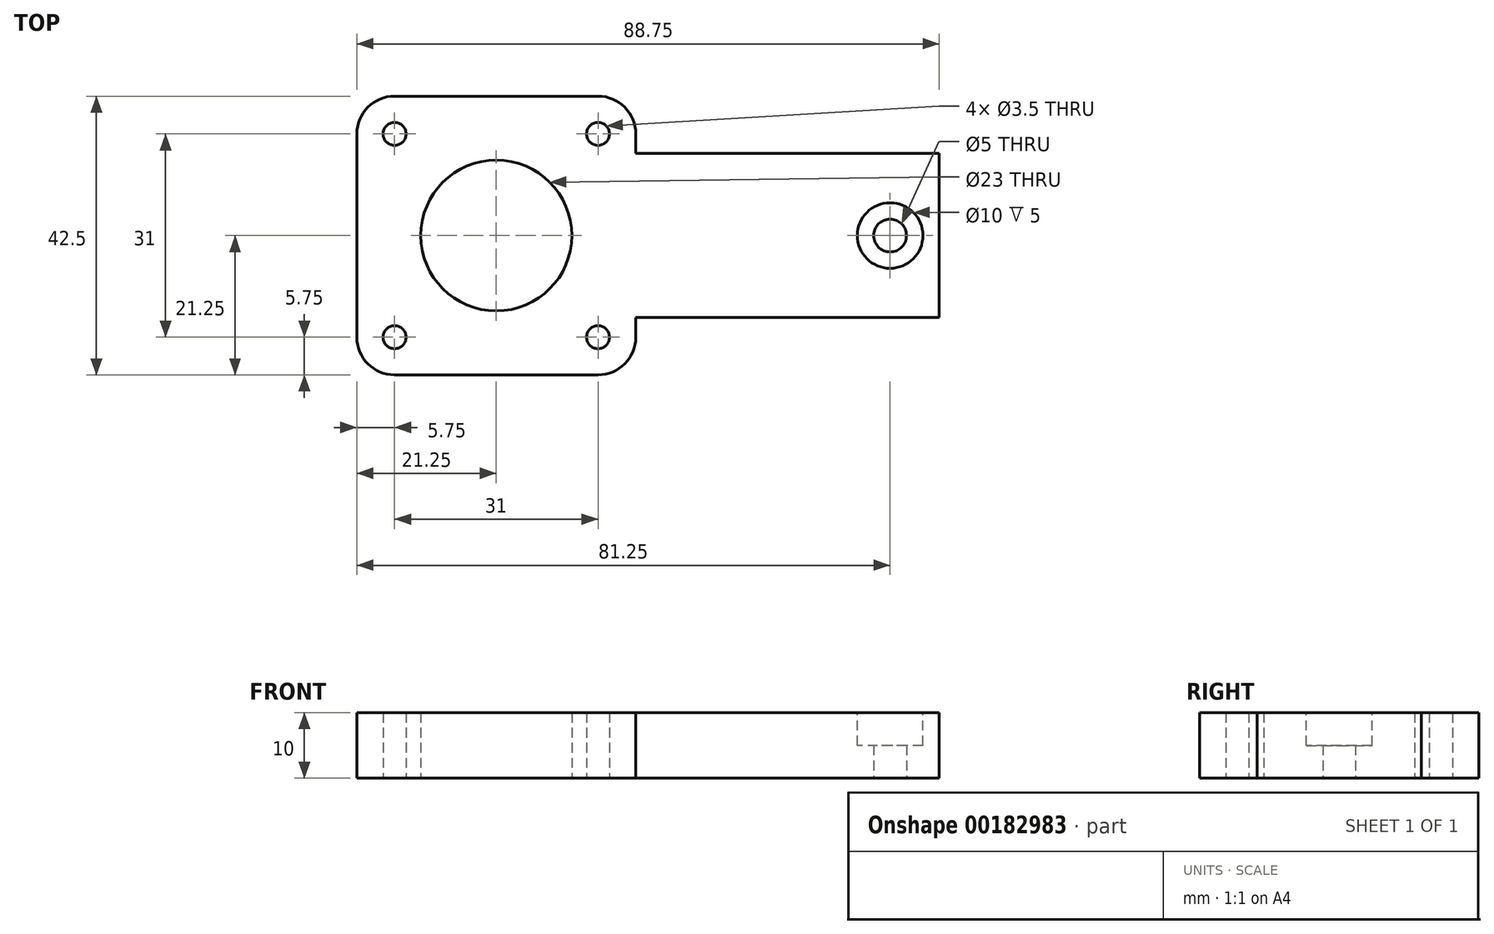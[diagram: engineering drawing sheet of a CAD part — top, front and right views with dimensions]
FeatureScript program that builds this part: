
annotation { "Feature Type Name" : "Feature", "Feature Type Description" : "" }
export const myFeature = defineFeature(function(context is Context, id is Id, definition is map)
    precondition{}
    {
        {
            var Q0;
            Q0=qCreatedBy(makeId("Top.planeOp"),FACE);
            var sketch = newSketch(context, id + "F0", { "sketchPlane" : qUnion([Q0])});
            skCircle(sketch, "E0", {"center": v(0, 0) * mm, "radius": 11.5 * mm});
            skCircle(sketch, "E1", {"center": v(-15.5, 15.5) * mm, "radius": 1.75 * mm});
            skCircle(sketch, "E2", {"center": v(15.5, 15.5) * mm, "radius": 1.75 * mm});
            skCircle(sketch, "E3", {"center": v(15.5, -15.5) * mm, "radius": 1.75 * mm});
            skCircle(sketch, "E4", {"center": v(-15.5, -15.5) * mm, "radius": 1.75 * mm});
            skLineSegment(sketch, "E5.bottom", {"start": v(-21.25, 21.25) * mm, "end": v(21.25, 21.25) * mm});
            skLineSegment(sketch, "E5.top", {"start": v(-21.25, -21.25) * mm, "end": v(21.25, -21.25) * mm});
            skLineSegment(sketch, "E5.left", {"start": v(-21.25, 21.25) * mm, "end": v(-21.25, -21.25) * mm});
            skLineSegment(sketch, "E5.right", {"start": v(21.25, 21.25) * mm, "end": v(21.25, -21.25) * mm});
            skPoint(sketch, "E6", {"position": v(21.25, 0) * mm});
            skCircle(sketch, "E7", {"center": v(60, 0) * mm, "radius": 2.5 * mm});
            skCircle(sketch, "E8", {"center": v(15.5, -15.5) * mm, "radius": 5.75 * mm});
            skCircle(sketch, "E9", {"center": v(15.5, 15.5) * mm, "radius": 5.75 * mm});
            skCircle(sketch, "E10", {"center": v(-15.5, 15.5) * mm, "radius": 5.75 * mm});
            skCircle(sketch, "E11", {"center": v(-15.5, -15.5) * mm, "radius": 5.75 * mm});
            skLineSegment(sketch, "E12.bottom", {"start": v(21.25, 12.5) * mm, "end": v(67.5, 12.5) * mm});
            skLineSegment(sketch, "E12.top", {"start": v(21.25, -12.5) * mm, "end": v(67.5, -12.5) * mm});
            skLineSegment(sketch, "E12.left", {"start": v(21.25, 12.5) * mm, "end": v(21.25, -12.5) * mm});
            skLineSegment(sketch, "E12.right", {"start": v(67.5, 12.5) * mm, "end": v(67.5, -12.5) * mm});
            skPoint(sketch, "E13", {"position": v(67.5, 0) * mm});
            skSolve(sketch);
        }
        {
            var Q0;
            Q0=makeQuery(id+"F0.imprint","IMPRINT",FACE,{"disambiguationData":[TD([[makeQuery(id+"F0.imprint","IMPRINT",EDGE,{"derivedFrom":sQuery(id+"F0.wireOp",EDGE,"E0")}),-1.0]])]});
            var Q1;
            Q1=makeQuery(id+"F0.imprint","IMPRINT",FACE,{"disambiguationData":[TD([[makeQuery(id+"F0.imprint","IMPRINT",EDGE,{"derivedFrom":sQuery(id+"F0.wireOp",EDGE,"E4")}),-1.0]])]});
            var Q2;
            Q2=makeQuery(id+"F0.imprint","IMPRINT",FACE,{"disambiguationData":[TD([[makeQuery(id+"F0.imprint","IMPRINT",EDGE,{"derivedFrom":sQuery(id+"F0.wireOp",EDGE,"E1")}),-1.0]])]});
            var Q3;
            Q3=makeQuery(id+"F0.imprint","IMPRINT",FACE,{"disambiguationData":[TD([[makeQuery(id+"F0.imprint","IMPRINT",EDGE,{"derivedFrom":sQuery(id+"F0.wireOp",EDGE,"E2")}),-1.0]])]});
            var Q4;
            Q4=makeQuery(id+"F0.imprint","IMPRINT",FACE,{"disambiguationData":[TD([[makeQuery(id+"F0.imprint","IMPRINT",EDGE,{"derivedFrom":sQuery(id+"F0.wireOp",EDGE,"E3")}),-1.0]])]});
            var Q5;
            Q5=makeQuery(id+"F0.imprint","IMPRINT",FACE,{"disambiguationData":[TD([[makeQuery(id+"F0.imprint","IMPRINT",EDGE,{"derivedFrom":sQuery(id+"F0.wireOp",EDGE,"rTMPlM7J-50n5-m7Sl-X2GD-EzflPRi3e04T.bottom")}),-1.0]])]});
            var Q6;
            Q6=makeQuery(id+"F0.imprint","IMPRINT",FACE,{"disambiguationData":[TD([[makeQuery(id+"F0.imprint","IMPRINT",EDGE,{"derivedFrom":sQuery(id+"F0.wireOp",EDGE,"E7")}),-1.0]])]});
            extrude(context, id + "F1", {"entities" : qUnion([Q0, Q1, Q2, Q3, Q4, Q5, Q6]), "depth" : 10 * mm});
        }
        {
            var Q0;
            Q0=makeQuery(id+"F1.opExtrude","CAP_FACE",FACE,{"disambiguationData":[OSD([sQuery(id+"F0.wireOp",EDGE,"E0"),sQuery(id+"F0.wireOp",EDGE,"E1"),sQuery(id+"F0.wireOp",EDGE,"E2"),sQuery(id+"F0.wireOp",EDGE,"E3"),sQuery(id+"F0.wireOp",EDGE,"E4"),sQuery(id+"F0.wireOp",EDGE,"E5.bottom"),sQuery(id+"F0.wireOp",EDGE,"E5.top"),sQuery(id+"F0.wireOp",EDGE,"E5.left"),sQuery(id+"F0.wireOp",EDGE,"E5.right"),sQuery(id+"F0.wireOp",EDGE,"E7"),sQuery(id+"F0.wireOp",EDGE,"E8"),sQuery(id+"F0.wireOp",EDGE,"E9"),sQuery(id+"F0.wireOp",EDGE,"E10"),sQuery(id+"F0.wireOp",EDGE,"E11"),sQuery(id+"F0.wireOp",EDGE,"E12.bottom"),sQuery(id+"F0.wireOp",EDGE,"E12.top"),sQuery(id+"F0.wireOp",EDGE,"E12.right")])],"isStart":false});
            var sketch = newSketch(context, id + "F2", { "sketchPlane" : qUnion([Q0])});
            skCircle(sketch, "E14", {"center": v(60, 0) * mm, "radius": 5 * mm});
            skSolve(sketch);
        }
        {
            var Q0;
            Q0=makeQuery(id+"F2.imprint","IMPRINT",FACE,{"disambiguationData":[TD([[makeQuery(id+"F2.imprint","IMPRINT",EDGE,{"derivedFrom":sQuery(id+"F2.wireOp",EDGE,"E14")}),1.0]])]});
            extrude(context, id + "F3", {"entities" : qUnion([Q0]), "operationType" : NewBodyOperationType.REMOVE, "oppositeDirection" : true, "depth" : 5 * mm});
        }
    });
